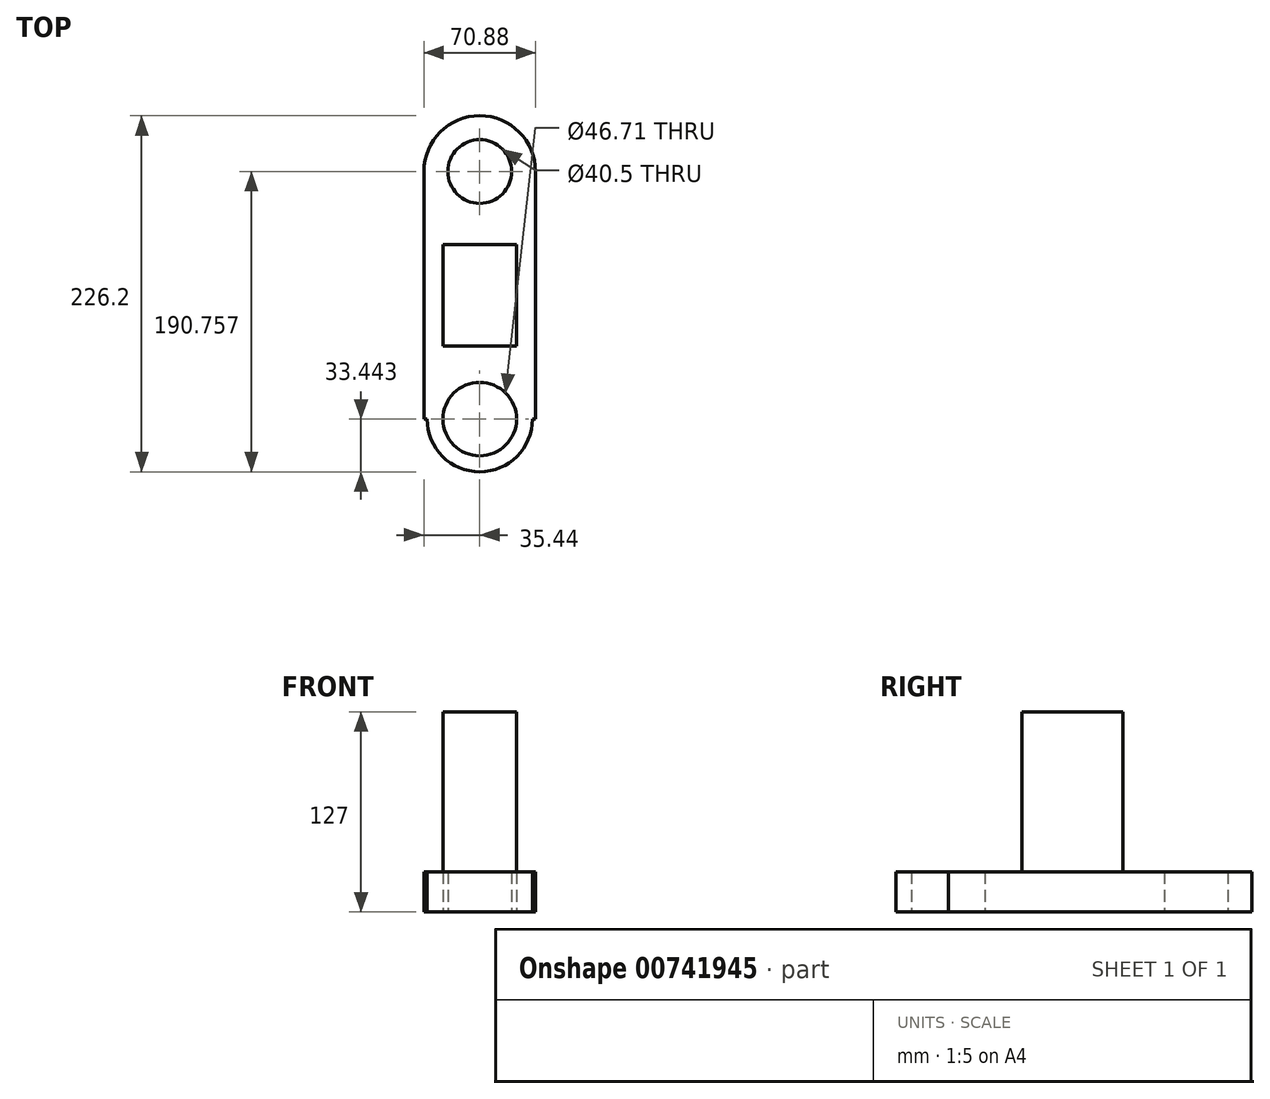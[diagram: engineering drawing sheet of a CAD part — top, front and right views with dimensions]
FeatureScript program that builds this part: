
annotation { "Feature Type Name" : "Feature", "Feature Type Description" : "" }
export const myFeature = defineFeature(function(context is Context, id is Id, definition is map)
    precondition{}
    {
        {
            var Q0;
            Q0=qCreatedBy(makeId("Top.planeOp"),FACE);
            var sketch = newSketch(context, id + "F0", { "sketchPlane" : qUnion([Q0])});
            skLineSegment(sketch, "E0.left", {"start": v(35.44, 78.66) * mm, "end": v(35.44, -78.66) * mm});
            skLineSegment(sketch, "E0.right", {"start": v(-35.44, 78.66) * mm, "end": v(-35.44, -78.66) * mm});
            skPoint(sketch, "E0.middle", {"position": v(0, 0) * mm});
            skArc(sketch, "E1", {"start": v(35.44, 78.66) * mm, "mid": v(0, 114.1) * mm, "end": v(-35.44, 78.66) * mm});
            skArc(sketch, "E2", {"start": v(-33.44, -78.66) * mm, "mid": v(0, -112.1) * mm, "end": v(33.44, -78.66) * mm});
            skLineSegment(sketch, "E3.bottom", {"start": v(23.43, -32.08) * mm, "end": v(-23.43, -32.08) * mm});
            skLineSegment(sketch, "E3.top", {"start": v(23.43, 32.08) * mm, "end": v(-23.43, 32.08) * mm});
            skLineSegment(sketch, "E3.left", {"start": v(23.43, -32.08) * mm, "end": v(23.43, 32.08) * mm});
            skLineSegment(sketch, "E3.right", {"start": v(-23.43, -32.08) * mm, "end": v(-23.43, 32.08) * mm});
            skCircle(sketch, "E4", {"center": v(0, -78.66) * mm, "radius": 23.36 * mm});
            skCircle(sketch, "E5", {"center": v(0, 78.66) * mm, "radius": 20.25 * mm});
            skCircle(sketch, "E6", {"center": v(0, 78.66) * mm, "radius": 12.52 * mm});
            skCircle(sketch, "E7", {"center": v(0, -78.66) * mm, "radius": 20.85 * mm});
            skLineSegment(sketch, "E8", {"start": v(33.44, -78.66) * mm, "end": v(35.44, -78.66) * mm});
            skLineSegment(sketch, "E9.trimOffspring", {"start": v(-33.44, -78.66) * mm, "end": v(-35.44, -78.66) * mm});
            skSolve(sketch);
        }
        {
            var Q0;
            Q0=makeQuery(id+"F0.imprint","IMPRINT",FACE,{"disambiguationData":[TD([[makeQuery(id+"F0.imprint","IMPRINT",EDGE,{"derivedFrom":sQuery(id+"F0.wireOp",EDGE,"E3.bottom")}),-1.0]])]});
            extrude(context, id + "F1", {"entities" : qUnion([Q0]), "depth" : 127 * mm, "offsetDistance" : 25.4 * mm});
        }
        {
            var Q0;
            {var subQ0=sQuery(id+"F0.wireOp",EDGE,"E1");Q0=makeQuery(id+"F0.imprint","IMPRINT",FACE,{"disambiguationData":[TD([[makeQuery(id+"F0.imprint","IMPRINT",EDGE,{"derivedFrom":subQ0}),1.0]])]});}
            var sketch = newSketch(context, id + "F2", { "sketchPlane" : qUnion([Q0])});
            skSolve(sketch);
        }
        {
            var Q0;
            Q0=makeQuery(id+"F0.imprint","IMPRINT",FACE,{"disambiguationData":[TD([[makeQuery(id+"F0.imprint","IMPRINT",EDGE,{"derivedFrom":sQuery(id+"F0.wireOp",EDGE,"E3.bottom")}),-1.0]])]});
            var Q1;
            Q1=makeQuery(id+"F2.imprint","IMPRINT",FACE,{"disambiguationData":[TD([[makeQuery(id+"F2.imprint","IMPRINT",EDGE,{"derivedFrom":makeQuery(id+"F0.imprint","IMPRINT",EDGE,{"derivedFrom":sQuery(id+"F0.wireOp",EDGE,"E0.left")})}),-1.0]])]});
            extrude(context, id + "F3", {"entities" : qUnion([Q0, Q1]), "operationType" : NewBodyOperationType.ADD, "depth" : 25.4 * mm, "offsetDistance" : 25.4 * mm});
        }
        {
            var Q0;
            Q0=makeQuery(id+"F1.opExtrude","SWEPT_FACE",FACE,{"disambiguationData":[OSD([sQuery(id+"F0.wireOp",EDGE,"E3.bottom")])]});
            var sketch = newSketch(context, id + "F4", { "sketchPlane" : qUnion([Q0])});
            skCircle(sketch, "E10", {"center": v(0, 70.85) * mm, "radius": 17.15 * mm});
            skSolve(sketch);
        }
        {
            var Q0;
            Q0=makeQuery(id+"F4.imprint","IMPRINT",FACE,{"disambiguationData":[TD([[makeQuery(id+"F4.imprint","IMPRINT",EDGE,{"derivedFrom":sQuery(id+"F4.wireOp",EDGE,"E10")}),1.0]])]});
            extrude(context, id + "F5", {"entities" : qUnion([Q0]), "operationType" : NewBodyOperationType.ADD, "oppositeDirection" : true, "depth" : 46.72 * mm, "offsetDistance" : 25.4 * mm});
        }
        {
            var Q0;
            Q0=qCreatedBy(makeId("Front.planeOp"),FACE);
            var sketch = newSketch(context, id + "F6", { "sketchPlane" : qUnion([Q0])});
            skCircle(sketch, "E11", {"center": v(0, 75.38) * mm, "radius": 19.17 * mm});
            skSolve(sketch);
        }
        {
            var Q0;
            Q0 = qSketchRegion(id + "F6", true);
            extrude(context, id + "F7", {"entities" : qUnion([Q0]), "operationType" : NewBodyOperationType.ADD, "oppositeDirection" : true, "depth" : 14.48 * mm, "offsetDistance" : 25.4 * mm});
        }
    });
